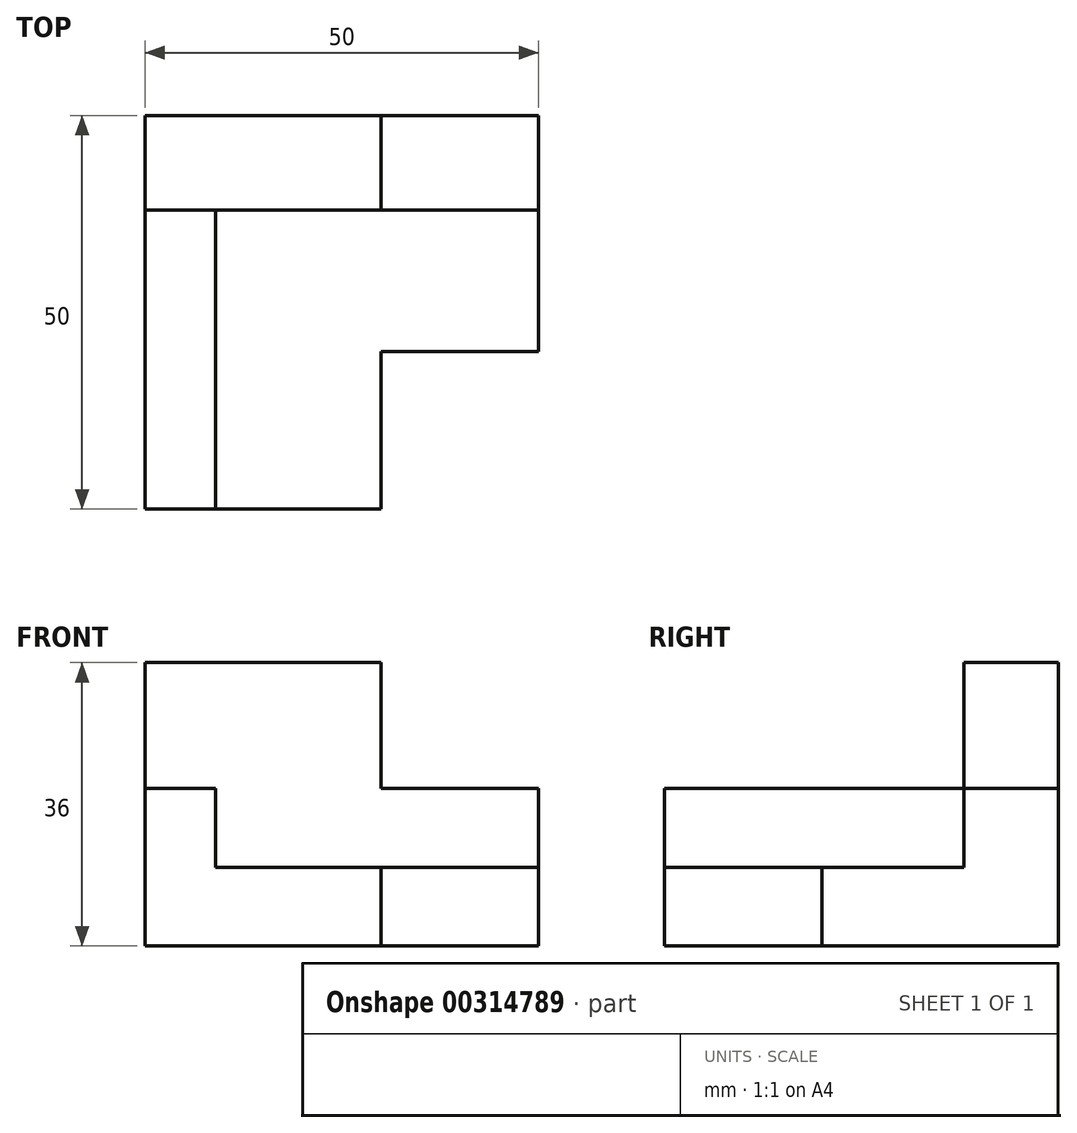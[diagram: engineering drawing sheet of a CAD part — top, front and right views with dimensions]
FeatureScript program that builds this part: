
annotation { "Feature Type Name" : "Feature", "Feature Type Description" : "" }
export const myFeature = defineFeature(function(context is Context, id is Id, definition is map)
    precondition{}
    {
        {
            var Q0;
            Q0=qCreatedBy(makeId("Top.planeOp"),FACE);
            var sketch = newSketch(context, id + "F0", { "sketchPlane" : qUnion([Q0])});
            skLineSegment(sketch, "E0.bottom", {"start": v(0, 0) * mm, "end": v(50, 0) * mm});
            skLineSegment(sketch, "E0.top", {"start": v(0, 50) * mm, "end": v(50, 50) * mm});
            skLineSegment(sketch, "E0.left", {"start": v(0, 0) * mm, "end": v(0, 50) * mm});
            skLineSegment(sketch, "E0.right", {"start": v(50, 0) * mm, "end": v(50, 50) * mm});
            skLineSegment(sketch, "E1.bottom", {"start": v(50, 0) * mm, "end": v(30, 0) * mm});
            skLineSegment(sketch, "E1.top", {"start": v(50, 20) * mm, "end": v(30, 20) * mm});
            skLineSegment(sketch, "E1.left", {"start": v(50, 0) * mm, "end": v(50, 20) * mm});
            skLineSegment(sketch, "E1.right", {"start": v(30, 0) * mm, "end": v(30, 20) * mm});
            skLineSegment(sketch, "E2", {"start": v(0, 38) * mm, "end": v(50, 38) * mm});
            skLineSegment(sketch, "E3", {"start": v(30, 38) * mm, "end": v(30, 50) * mm});
            skLineSegment(sketch, "E4", {"start": v(9, 38) * mm, "end": v(9, 0) * mm});
            skSolve(sketch);
        }
        {
            var Q0;
            {var subQ0=sQuery(id+"F0.wireOp",EDGE,"E4");Q0=makeQuery(id+"F0.imprint","IMPRINT",FACE,{"disambiguationData":[TD([[makeQuery(id+"F0.imprint","IMPRINT",EDGE,{"derivedFrom":subQ0}),-1.0]])]});}
            var Q1;
            {var subQ3=sQuery(id+"F0.wireOp",EDGE,"E3");Q1=makeQuery(id+"F0.imprint","IMPRINT",FACE,{"disambiguationData":[TD([[makeQuery(id+"F0.imprint","IMPRINT",EDGE,{"derivedFrom":subQ3}),-1.0]])]});}
            var Q2;
            {var subQ6=sQuery(id+"F0.wireOp",EDGE,"E3");Q2=makeQuery(id+"F0.imprint","IMPRINT",FACE,{"disambiguationData":[TD([[makeQuery(id+"F0.imprint","IMPRINT",EDGE,{"derivedFrom":subQ6}),1.0]])]});}
            var Q3;
            {var subQ3=sQuery(id+"F0.wireOp",EDGE,"E1.top");Q3=makeQuery(id+"F0.imprint","IMPRINT",FACE,{"disambiguationData":[TD([[makeQuery(id+"F0.imprint","IMPRINT",EDGE,{"derivedFrom":subQ3}),-1.0]])]});}
            extrude(context, id + "F1", {"entities" : qUnion([Q0, Q1, Q2, Q3]), "depth" : 10 * mm});
        }
        {
            var Q0;
            {var subQ0=sQuery(id+"F0.wireOp",EDGE,"E4");Q0=makeQuery(id+"F0.imprint","IMPRINT",FACE,{"disambiguationData":[TD([[makeQuery(id+"F0.imprint","IMPRINT",EDGE,{"derivedFrom":subQ0}),-1.0]])]});}
            var Q1;
            {var subQ6=sQuery(id+"F0.wireOp",EDGE,"E3");Q1=makeQuery(id+"F0.imprint","IMPRINT",FACE,{"disambiguationData":[TD([[makeQuery(id+"F0.imprint","IMPRINT",EDGE,{"derivedFrom":subQ6}),1.0]])]});}
            var Q2;
            {var subQ3=sQuery(id+"F0.wireOp",EDGE,"E3");Q2=makeQuery(id+"F0.imprint","IMPRINT",FACE,{"disambiguationData":[TD([[makeQuery(id+"F0.imprint","IMPRINT",EDGE,{"derivedFrom":subQ3}),-1.0]])]});}
            extrude(context, id + "F2", {"entities" : qUnion([Q0, Q1, Q2]), "operationType" : NewBodyOperationType.ADD, "depth" : 20 * mm});
        }
        {
            var Q0;
            {var subQ6=sQuery(id+"F0.wireOp",EDGE,"E3");Q0=makeQuery(id+"F0.imprint","IMPRINT",FACE,{"disambiguationData":[TD([[makeQuery(id+"F0.imprint","IMPRINT",EDGE,{"derivedFrom":subQ6}),1.0]])]});}
            extrude(context, id + "F3", {"entities" : qUnion([Q0]), "operationType" : NewBodyOperationType.ADD, "depth" : 36 * mm});
        }
    });
